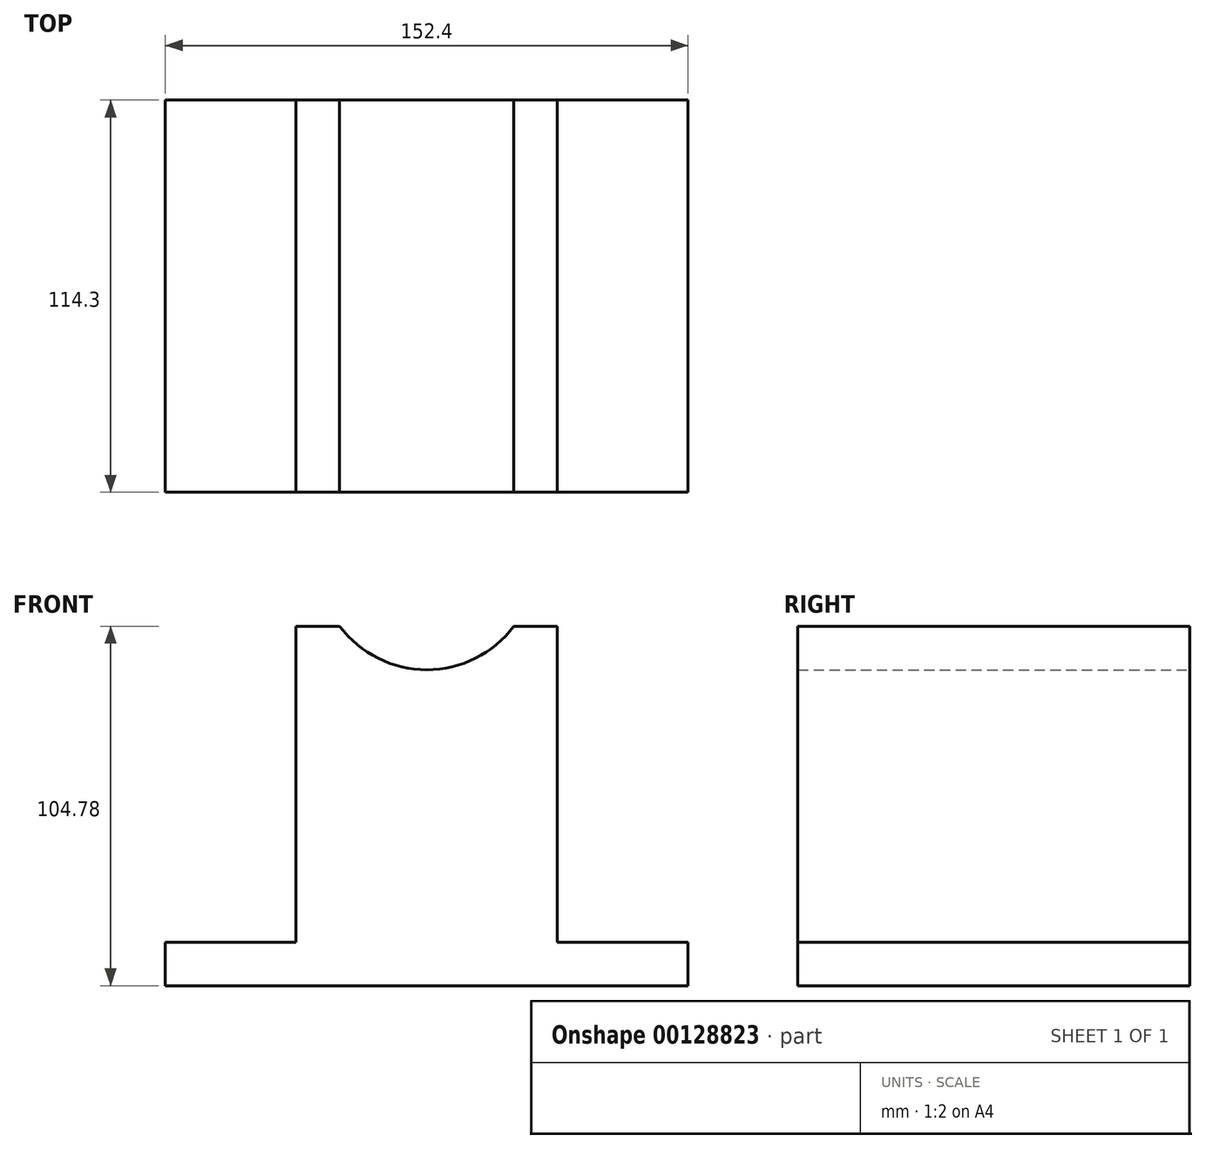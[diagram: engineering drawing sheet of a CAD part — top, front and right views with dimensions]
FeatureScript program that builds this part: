
annotation { "Feature Type Name" : "Feature", "Feature Type Description" : "" }
export const myFeature = defineFeature(function(context is Context, id is Id, definition is map)
    precondition{}
    {
        {
            var Q0;
            Q0=qCreatedBy(makeId("Front.planeOp"),FACE);
            var sketch = newSketch(context, id + "F0", { "sketchPlane" : qUnion([Q0])});
            skLineSegment(sketch, "E0", {"start": v(0, 0) * mm, "end": v(0, 12.7) * mm});
            skLineSegment(sketch, "E1", {"start": v(0, 0) * mm, "end": v(152.4, 0) * mm});
            skLineSegment(sketch, "E2", {"start": v(152.4, 0) * mm, "end": v(152.4, 12.7) * mm});
            skLineSegment(sketch, "E3", {"start": v(0, 12.7) * mm, "end": v(38.1, 12.7) * mm});
            skLineSegment(sketch, "E4", {"start": v(152.4, 12.7) * mm, "end": v(114.3, 12.7) * mm});
            skLineSegment(sketch, "E5", {"start": v(38.1, 12.7) * mm, "end": v(38.1, 104.78) * mm});
            skLineSegment(sketch, "E6", {"start": v(114.3, 12.7) * mm, "end": v(114.3, 104.78) * mm});
            skLineSegment(sketch, "E7", {"start": v(38.1, 104.78) * mm, "end": v(50.8, 104.78) * mm});
            skLineSegment(sketch, "E8", {"start": v(114.3, 104.78) * mm, "end": v(101.6, 104.78) * mm});
            skArc(sketch, "E9", {"start": v(50.8, 104.78) * mm, "mid": v(76.2, 92.08) * mm, "end": v(101.6, 104.78) * mm});
            skSolve(sketch);
        }
        {
            var Q0;
            Q0=makeQuery(id+"F0.imprint","IMPRINT",FACE,{"disambiguationData":[TD([[makeQuery(id+"F0.imprint","IMPRINT",EDGE,{"derivedFrom":sQuery(id+"F0.wireOp",EDGE,"E0")}),-1.0]])]});
            extrude(context, id + "F1", {"entities" : qUnion([Q0]), "depth" : 114.3 * mm});
        }
    });
